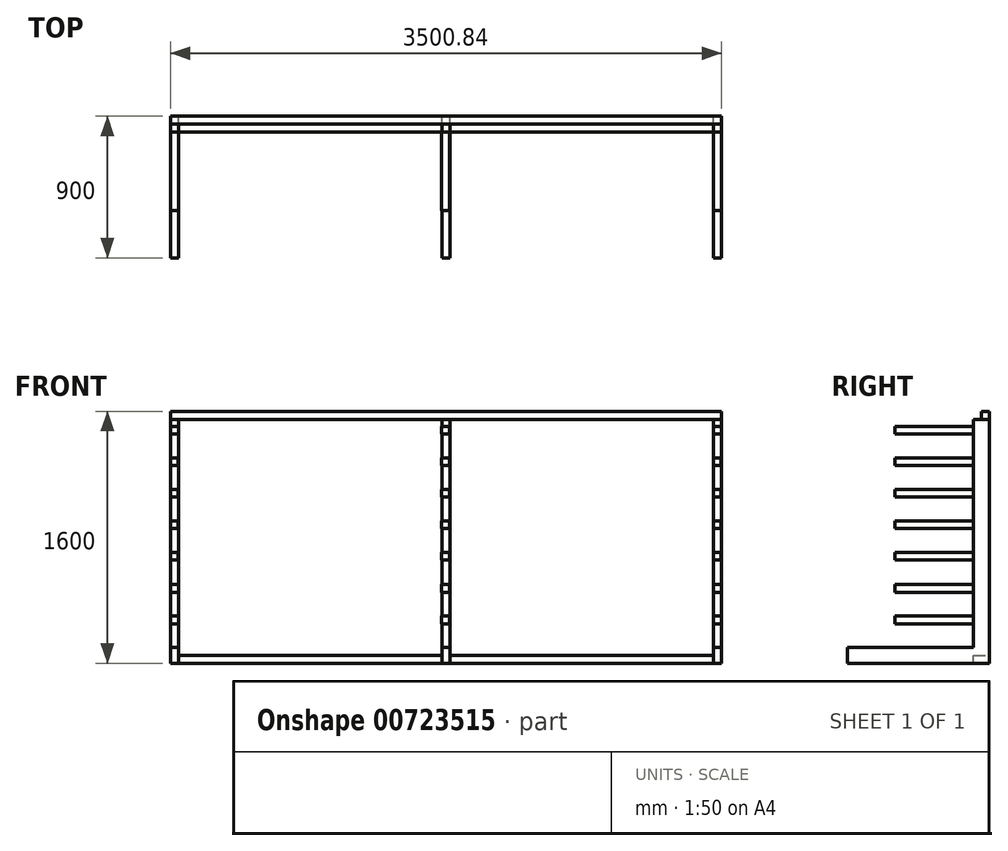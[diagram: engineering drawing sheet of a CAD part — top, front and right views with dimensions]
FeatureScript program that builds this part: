
annotation { "Feature Type Name" : "Feature", "Feature Type Description" : "" }
export const myFeature = defineFeature(function(context is Context, id is Id, definition is map)
    precondition{}
    {
        {
            var Q0;
            Q0=qCreatedBy(makeId("Front.planeOp"),FACE);
            var sketch = newSketch(context, id + "F0", { "sketchPlane" : qUnion([Q0])});
            skLineSegment(sketch, "E0.bottom", {"start": v(0, 0) * mm, "end": v(-3500, 0) * mm});
            skLineSegment(sketch, "E0.left", {"start": v(0, 0) * mm, "end": v(0, 1550) * mm});
            skLineSegment(sketch, "E0.right", {"start": v(-3500, 0) * mm, "end": v(-3500, 1550) * mm});
            skLineSegment(sketch, "E1.1", {"start": v(-50, 50) * mm, "end": v(-50, 1550) * mm});
            skLineSegment(sketch, "E1.2", {"start": v(-50, 50) * mm, "end": v(-1725, 50) * mm});
            skLineSegment(sketch, "E1.3", {"start": v(-3450, 50) * mm, "end": v(-3450, 1550) * mm});
            skPoint(sketch, "E2", {"position": v(-1775, 50) * mm});
            skPoint(sketch, "E3", {"position": v(-1725, 50) * mm});
            skLineSegment(sketch, "E4", {"start": v(-1775, 50) * mm, "end": v(-1775, 1550) * mm});
            skLineSegment(sketch, "E5.0", {"start": v(-1725, 50) * mm, "end": v(-1725, 1550) * mm});
            skLineSegment(sketch, "E6.trimOffspring", {"start": v(-1775, 50) * mm, "end": v(-3450, 50) * mm});
            skLineSegment(sketch, "E7", {"start": v(-3450, 1550) * mm, "end": v(-3500, 1550) * mm});
            skLineSegment(sketch, "E8", {"start": v(-1775, 1550) * mm, "end": v(-1725, 1550) * mm});
            skLineSegment(sketch, "E9", {"start": v(-50, 1550) * mm, "end": v(0, 1550) * mm});
            skSolve(sketch);
        }
        {
            var Q0;
            Q0=makeQuery(id+"F0.imprint","IMPRINT",FACE,{"disambiguationData":[TD([[makeQuery(id+"F0.imprint","IMPRINT",EDGE,{"derivedFrom":sQuery(id+"F0.wireOp",EDGE,"E0.bottom")}),-1.0]])]});
            extrude(context, id + "F1", {"entities" : qUnion([Q0]), "depth" : 100 * mm, "offsetDistance" : 25 * mm});
        }
        {
            var Q0;
            Q0=makeQuery(id+"F1.opExtrude","CAP_FACE",FACE,{"disambiguationData":[OSD([sQuery(id+"F0.wireOp",EDGE,"E0.bottom"),sQuery(id+"F0.wireOp",EDGE,"E0.left"),sQuery(id+"F0.wireOp",EDGE,"E0.right"),sQuery(id+"F0.wireOp",EDGE,"E1.1"),sQuery(id+"F0.wireOp",EDGE,"E1.2"),sQuery(id+"F0.wireOp",EDGE,"E1.3"),sQuery(id+"F0.wireOp",EDGE,"E4"),sQuery(id+"F0.wireOp",EDGE,"E5.0"),sQuery(id+"F0.wireOp",EDGE,"E6.trimOffspring"),sQuery(id+"F0.wireOp",EDGE,"E7"),sQuery(id+"F0.wireOp",EDGE,"E8"),sQuery(id+"F0.wireOp",EDGE,"E9")])],"isStart":false});
            var sketch = newSketch(context, id + "F2", { "sketchPlane" : qUnion([Q0])});
            skLineSegment(sketch, "E10.bottom", {"start": v(-3500, 0) * mm, "end": v(-3450, 0) * mm});
            skLineSegment(sketch, "E10.top", {"start": v(-3500, 100) * mm, "end": v(-3450, 100) * mm});
            skLineSegment(sketch, "E10.left", {"start": v(-3500, 0) * mm, "end": v(-3500, 100) * mm});
            skLineSegment(sketch, "E10.right", {"start": v(-3450, 0) * mm, "end": v(-3450, 100) * mm});
            skLineSegment(sketch, "E11.bottom", {"start": v(-1775, 0) * mm, "end": v(-1725, 0) * mm});
            skLineSegment(sketch, "E11.top", {"start": v(-1775, 100) * mm, "end": v(-1725, 100) * mm});
            skLineSegment(sketch, "E11.left", {"start": v(-1775, 0) * mm, "end": v(-1775, 100) * mm});
            skLineSegment(sketch, "E11.right", {"start": v(-1725, 0) * mm, "end": v(-1725, 100) * mm});
            skLineSegment(sketch, "E12.bottom", {"start": v(0, 0) * mm, "end": v(-50, 0) * mm});
            skLineSegment(sketch, "E12.top", {"start": v(0, 100) * mm, "end": v(-50, 100) * mm});
            skLineSegment(sketch, "E12.left", {"start": v(0, 0) * mm, "end": v(0, 100) * mm});
            skLineSegment(sketch, "E12.right", {"start": v(-50, 0) * mm, "end": v(-50, 100) * mm});
            skSolve(sketch);
        }
        {
            var Q0;
            {var subQ2=sQuery(id+"F2.wireOp",EDGE,"E11.bottom");Q0=makeQuery(id+"F2.imprint","IMPRINT",FACE,{"disambiguationData":[TD([[makeQuery(id+"F2.imprint","IMPRINT",EDGE,{"derivedFrom":subQ2}),-1.0]])]});}
            var Q1;
            {var subQ3=sQuery(id+"F2.wireOp",EDGE,"E10.bottom");Q1=makeQuery(id+"F2.imprint","IMPRINT",FACE,{"disambiguationData":[TD([[makeQuery(id+"F2.imprint","IMPRINT",EDGE,{"derivedFrom":subQ3}),-1.0]])]});}
            var Q2;
            {var subQ3=sQuery(id+"F2.wireOp",EDGE,"E12.bottom");Q2=makeQuery(id+"F2.imprint","IMPRINT",FACE,{"disambiguationData":[TD([[makeQuery(id+"F2.imprint","IMPRINT",EDGE,{"derivedFrom":subQ3}),-1.0]])]});}
            extrude(context, id + "F3", {"entities" : qUnion([Q0, Q1, Q2]), "operationType" : NewBodyOperationType.ADD, "depth" : 800 * mm, "offsetDistance" : 25 * mm});
        }
        {
            var Q0;
            Q0=makeQuery(id+"F1.opExtrude","SWEPT_FACE",FACE,{"disambiguationData":[OSD([sQuery(id+"F0.wireOp",EDGE,"E8")])]});
            var sketch = newSketch(context, id + "F4", { "sketchPlane" : qUnion([Q0])});
            skPoint(sketch, "E13", {"position": v(-1750, 0) * mm});
            skPoint(sketch, "E14", {"position": v(-1750, -100) * mm});
            skLineSegment(sketch, "E15", {"start": v(-1750, 0) * mm, "end": v(-1750, -50) * mm});
            skLineSegment(sketch, "E16.bottom", {"start": v(-1750, -50) * mm, "end": v(-3499.82, -50) * mm});
            skLineSegment(sketch, "E16.top", {"start": v(-1750, 0) * mm, "end": v(-3499.82, 0) * mm});
            skLineSegment(sketch, "E16.left", {"start": v(-1750, -50) * mm, "end": v(-1750, 0) * mm});
            skLineSegment(sketch, "E16.right", {"start": v(-3499.82, -50) * mm, "end": v(-3499.82, 0) * mm});
            skLineSegment(sketch, "E17.MirrorCS", {"start": v(-1750, 0) * mm, "end": v(-0.18, 0) * mm});
            skLineSegment(sketch, "E18.MirrorCS", {"start": v(-1750, -50) * mm, "end": v(-0.18, -50) * mm});
            skLineSegment(sketch, "E19.MirrorCS", {"start": v(-0.18, -50) * mm, "end": v(-0.18, 0) * mm});
            skSolve(sketch);
        }
        {
            var Q0;
            Q0=qSketchRegion(id+"F4",true);
            extrude(context, id + "F5", {"entities" : qUnion([Q0]), "operationType" : NewBodyOperationType.ADD, "depth" : 50 * mm, "offsetDistance" : 25 * mm});
        }
        {
            var Q0;
            {var subQ0=sQuery(id+"F0.wireOp",EDGE,"E0.right");var subQ1=sQuery(id+"F0.wireOp",EDGE,"E7");var subQ2=sQuery(id+"F0.wireOp",EDGE,"E1.3");Q0=makeQuery(id+"F3.boolean.opBoolean","SPLIT",FACE,{"disambiguationData":[TD([makeQuery(id+"F1.opExtrude","SWEPT_FACE",FACE,{"disambiguationData":[OSD([subQ0])]})])],"derivedFrom":makeQuery(id+"F1.opExtrude","CAP_FACE",FACE,{"disambiguationData":[OSD([sQuery(id+"F0.wireOp",EDGE,"E0.bottom"),sQuery(id+"F0.wireOp",EDGE,"E0.left"),subQ0,sQuery(id+"F0.wireOp",EDGE,"E1.1"),sQuery(id+"F0.wireOp",EDGE,"E1.2"),subQ2,sQuery(id+"F0.wireOp",EDGE,"E4"),sQuery(id+"F0.wireOp",EDGE,"E5.0"),sQuery(id+"F0.wireOp",EDGE,"E6.trimOffspring"),subQ1,sQuery(id+"F0.wireOp",EDGE,"E8"),sQuery(id+"F0.wireOp",EDGE,"E9")])],"isStart":false})});}
            var sketch = newSketch(context, id + "F6", { "sketchPlane" : qUnion([Q0])});
            skLineSegment(sketch, "E20.bottom", {"start": v(-3500, 250) * mm, "end": v(-3450, 250) * mm});
            skLineSegment(sketch, "E20.top", {"start": v(-3500, 300) * mm, "end": v(-3450, 300) * mm});
            skLineSegment(sketch, "E20.left", {"start": v(-3500, 250) * mm, "end": v(-3500, 300) * mm});
            skLineSegment(sketch, "E20.right", {"start": v(-3450, 250) * mm, "end": v(-3450, 300) * mm});
            skPoint(sketch, "E21", {"position": v(-3500, 450) * mm});
            skLineSegment(sketch, "E22.bottom", {"start": v(-3500, 450) * mm, "end": v(-3450, 450) * mm});
            skLineSegment(sketch, "E22.top", {"start": v(-3500, 500) * mm, "end": v(-3450, 500) * mm});
            skLineSegment(sketch, "E22.left", {"start": v(-3500, 450) * mm, "end": v(-3500, 500) * mm});
            skLineSegment(sketch, "E22.right", {"start": v(-3450, 450) * mm, "end": v(-3450, 500) * mm});
            skPoint(sketch, "E23", {"position": v(-3500, 650) * mm});
            skPoint(sketch, "E24", {"position": v(-3500.84, 655.24) * mm});
            skPoint(sketch, "E25", {"position": v(-3500.84, 855.24) * mm});
            skPoint(sketch, "E26", {"position": v(-3500.84, 1055.24) * mm});
            skPoint(sketch, "E27", {"position": v(-3500.84, 1255.24) * mm});
            skLineSegment(sketch, "E28.bottom", {"start": v(-3500.84, 655.24) * mm, "end": v(-3450.84, 655.24) * mm});
            skLineSegment(sketch, "E28.top", {"start": v(-3500.84, 705.24) * mm, "end": v(-3450.84, 705.24) * mm});
            skLineSegment(sketch, "E28.left", {"start": v(-3500.84, 655.24) * mm, "end": v(-3500.84, 705.24) * mm});
            skLineSegment(sketch, "E28.right", {"start": v(-3450.84, 655.24) * mm, "end": v(-3450.84, 705.24) * mm});
            skLineSegment(sketch, "E29.bottom", {"start": v(-3500.84, 855.24) * mm, "end": v(-3450.84, 855.24) * mm});
            skLineSegment(sketch, "E29.top", {"start": v(-3500.84, 905.24) * mm, "end": v(-3450.84, 905.24) * mm});
            skLineSegment(sketch, "E29.left", {"start": v(-3500.84, 855.24) * mm, "end": v(-3500.84, 905.24) * mm});
            skLineSegment(sketch, "E29.right", {"start": v(-3450.84, 855.24) * mm, "end": v(-3450.84, 905.24) * mm});
            skLineSegment(sketch, "E30.bottom", {"start": v(-3500.84, 1055.24) * mm, "end": v(-3450.84, 1055.24) * mm});
            skLineSegment(sketch, "E30.top", {"start": v(-3500.84, 1105.24) * mm, "end": v(-3450.84, 1105.24) * mm});
            skLineSegment(sketch, "E30.left", {"start": v(-3500.84, 1055.24) * mm, "end": v(-3500.84, 1105.24) * mm});
            skLineSegment(sketch, "E30.right", {"start": v(-3450.84, 1055.24) * mm, "end": v(-3450.84, 1105.24) * mm});
            skLineSegment(sketch, "E31.bottom", {"start": v(-3500.84, 1255.24) * mm, "end": v(-3450.84, 1255.24) * mm});
            skLineSegment(sketch, "E31.top", {"start": v(-3500.84, 1305.24) * mm, "end": v(-3450.84, 1305.24) * mm});
            skLineSegment(sketch, "E31.left", {"start": v(-3500.84, 1255.24) * mm, "end": v(-3500.84, 1305.24) * mm});
            skLineSegment(sketch, "E31.right", {"start": v(-3450.84, 1255.24) * mm, "end": v(-3450.84, 1305.24) * mm});
            skPoint(sketch, "E32", {"position": v(-3500, 1455.24) * mm});
            skLineSegment(sketch, "E33.bottom", {"start": v(-3500, 1455.24) * mm, "end": v(-3450, 1455.24) * mm});
            skLineSegment(sketch, "E33.top", {"start": v(-3500, 1505.24) * mm, "end": v(-3450, 1505.24) * mm});
            skLineSegment(sketch, "E33.left", {"start": v(-3500, 1455.24) * mm, "end": v(-3500, 1505.24) * mm});
            skLineSegment(sketch, "E33.right", {"start": v(-3450, 1455.24) * mm, "end": v(-3450, 1505.24) * mm});
            skPoint(sketch, "E34", {"position": v(-52.24, 250) * mm});
            skPoint(sketch, "E35", {"position": v(-1777.89, 250) * mm});
            skLineSegment(sketch, "E36.bottom", {"start": v(-1777.89, 250) * mm, "end": v(-1727.89, 250) * mm});
            skLineSegment(sketch, "E36.top", {"start": v(-1777.89, 300) * mm, "end": v(-1727.89, 300) * mm});
            skLineSegment(sketch, "E36.left", {"start": v(-1777.89, 250) * mm, "end": v(-1777.89, 300) * mm});
            skLineSegment(sketch, "E36.right", {"start": v(-1727.89, 250) * mm, "end": v(-1727.89, 300) * mm});
            skPoint(sketch, "E37", {"position": v(-1777.89, 450) * mm});
            skLineSegment(sketch, "E38.bottom", {"start": v(-1777.89, 450) * mm, "end": v(-1727.89, 450) * mm});
            skLineSegment(sketch, "E38.top", {"start": v(-1777.89, 500) * mm, "end": v(-1727.89, 500) * mm});
            skLineSegment(sketch, "E38.left", {"start": v(-1777.89, 450) * mm, "end": v(-1777.89, 500) * mm});
            skLineSegment(sketch, "E38.right", {"start": v(-1727.89, 450) * mm, "end": v(-1727.89, 500) * mm});
            skPoint(sketch, "E39", {"position": v(-1777.89, 650) * mm});
            skPoint(sketch, "E40", {"position": v(-1778.73, 655.24) * mm});
            skPoint(sketch, "E41", {"position": v(-1778.73, 855.24) * mm});
            skPoint(sketch, "E42", {"position": v(-1778.73, 1055.24) * mm});
            skPoint(sketch, "E43", {"position": v(-1778.73, 1255.24) * mm});
            skLineSegment(sketch, "E44.bottom", {"start": v(-1778.73, 655.24) * mm, "end": v(-1728.73, 655.24) * mm});
            skLineSegment(sketch, "E44.top", {"start": v(-1778.73, 705.24) * mm, "end": v(-1728.73, 705.24) * mm});
            skLineSegment(sketch, "E44.left", {"start": v(-1778.73, 655.24) * mm, "end": v(-1778.73, 705.24) * mm});
            skLineSegment(sketch, "E44.right", {"start": v(-1728.73, 655.24) * mm, "end": v(-1728.73, 705.24) * mm});
            skLineSegment(sketch, "E45.bottom", {"start": v(-1778.73, 855.24) * mm, "end": v(-1728.73, 855.24) * mm});
            skLineSegment(sketch, "E45.top", {"start": v(-1778.73, 905.24) * mm, "end": v(-1728.73, 905.24) * mm});
            skLineSegment(sketch, "E45.left", {"start": v(-1778.73, 855.24) * mm, "end": v(-1778.73, 905.24) * mm});
            skLineSegment(sketch, "E45.right", {"start": v(-1728.73, 855.24) * mm, "end": v(-1728.73, 905.24) * mm});
            skLineSegment(sketch, "E46.bottom", {"start": v(-1778.73, 1055.24) * mm, "end": v(-1728.73, 1055.24) * mm});
            skLineSegment(sketch, "E46.top", {"start": v(-1778.73, 1105.24) * mm, "end": v(-1728.73, 1105.24) * mm});
            skLineSegment(sketch, "E46.left", {"start": v(-1778.73, 1055.24) * mm, "end": v(-1778.73, 1105.24) * mm});
            skLineSegment(sketch, "E46.right", {"start": v(-1728.73, 1055.24) * mm, "end": v(-1728.73, 1105.24) * mm});
            skLineSegment(sketch, "E47.bottom", {"start": v(-1778.73, 1255.24) * mm, "end": v(-1728.73, 1255.24) * mm});
            skLineSegment(sketch, "E47.top", {"start": v(-1778.73, 1305.24) * mm, "end": v(-1728.73, 1305.24) * mm});
            skLineSegment(sketch, "E47.left", {"start": v(-1778.73, 1255.24) * mm, "end": v(-1778.73, 1305.24) * mm});
            skLineSegment(sketch, "E47.right", {"start": v(-1728.73, 1255.24) * mm, "end": v(-1728.73, 1305.24) * mm});
            skPoint(sketch, "E48", {"position": v(-1777.89, 1455.24) * mm});
            skLineSegment(sketch, "E49.bottom", {"start": v(-1777.89, 1455.24) * mm, "end": v(-1727.89, 1455.24) * mm});
            skLineSegment(sketch, "E49.top", {"start": v(-1777.89, 1505.24) * mm, "end": v(-1727.89, 1505.24) * mm});
            skLineSegment(sketch, "E49.left", {"start": v(-1777.89, 1455.24) * mm, "end": v(-1777.89, 1505.24) * mm});
            skLineSegment(sketch, "E49.right", {"start": v(-1727.89, 1455.24) * mm, "end": v(-1727.89, 1505.24) * mm});
            skLineSegment(sketch, "E50.bottom", {"start": v(-52.24, 250) * mm, "end": v(-2.24, 250) * mm});
            skLineSegment(sketch, "E50.top", {"start": v(-52.24, 300) * mm, "end": v(-2.24, 300) * mm});
            skLineSegment(sketch, "E50.left", {"start": v(-52.24, 250) * mm, "end": v(-52.24, 300) * mm});
            skLineSegment(sketch, "E50.right", {"start": v(-2.24, 250) * mm, "end": v(-2.24, 300) * mm});
            skPoint(sketch, "E51", {"position": v(-52.24, 450) * mm});
            skLineSegment(sketch, "E52.bottom", {"start": v(-52.24, 450) * mm, "end": v(-2.24, 450) * mm});
            skLineSegment(sketch, "E52.top", {"start": v(-52.24, 500) * mm, "end": v(-2.24, 500) * mm});
            skLineSegment(sketch, "E52.left", {"start": v(-52.24, 450) * mm, "end": v(-52.24, 500) * mm});
            skLineSegment(sketch, "E52.right", {"start": v(-2.24, 450) * mm, "end": v(-2.24, 500) * mm});
            skPoint(sketch, "E53", {"position": v(-52.24, 650) * mm});
            skPoint(sketch, "E54", {"position": v(-53.08, 655.24) * mm});
            skPoint(sketch, "E55", {"position": v(-53.08, 855.24) * mm});
            skPoint(sketch, "E56", {"position": v(-53.08, 1055.24) * mm});
            skPoint(sketch, "E57", {"position": v(-53.08, 1255.24) * mm});
            skLineSegment(sketch, "E58.bottom", {"start": v(-53.08, 655.24) * mm, "end": v(-3.08, 655.24) * mm});
            skLineSegment(sketch, "E58.top", {"start": v(-53.08, 705.24) * mm, "end": v(-3.08, 705.24) * mm});
            skLineSegment(sketch, "E58.left", {"start": v(-53.08, 655.24) * mm, "end": v(-53.08, 705.24) * mm});
            skLineSegment(sketch, "E58.right", {"start": v(-3.08, 655.24) * mm, "end": v(-3.08, 705.24) * mm});
            skLineSegment(sketch, "E59.bottom", {"start": v(-53.08, 855.24) * mm, "end": v(-3.08, 855.24) * mm});
            skLineSegment(sketch, "E59.top", {"start": v(-53.08, 905.24) * mm, "end": v(-3.08, 905.24) * mm});
            skLineSegment(sketch, "E59.left", {"start": v(-53.08, 855.24) * mm, "end": v(-53.08, 905.24) * mm});
            skLineSegment(sketch, "E59.right", {"start": v(-3.08, 855.24) * mm, "end": v(-3.08, 905.24) * mm});
            skLineSegment(sketch, "E60.bottom", {"start": v(-53.08, 1055.24) * mm, "end": v(-3.08, 1055.24) * mm});
            skLineSegment(sketch, "E60.top", {"start": v(-53.08, 1105.24) * mm, "end": v(-3.08, 1105.24) * mm});
            skLineSegment(sketch, "E60.left", {"start": v(-53.08, 1055.24) * mm, "end": v(-53.08, 1105.24) * mm});
            skLineSegment(sketch, "E60.right", {"start": v(-3.08, 1055.24) * mm, "end": v(-3.08, 1105.24) * mm});
            skLineSegment(sketch, "E61.bottom", {"start": v(-53.08, 1255.24) * mm, "end": v(-3.08, 1255.24) * mm});
            skLineSegment(sketch, "E61.top", {"start": v(-53.08, 1305.24) * mm, "end": v(-3.08, 1305.24) * mm});
            skLineSegment(sketch, "E61.left", {"start": v(-53.08, 1255.24) * mm, "end": v(-53.08, 1305.24) * mm});
            skLineSegment(sketch, "E61.right", {"start": v(-3.08, 1255.24) * mm, "end": v(-3.08, 1305.24) * mm});
            skPoint(sketch, "E62", {"position": v(-52.24, 1455.24) * mm});
            skLineSegment(sketch, "E63.bottom", {"start": v(-52.24, 1455.24) * mm, "end": v(-2.24, 1455.24) * mm});
            skLineSegment(sketch, "E63.top", {"start": v(-52.24, 1505.24) * mm, "end": v(-2.24, 1505.24) * mm});
            skLineSegment(sketch, "E63.left", {"start": v(-52.24, 1455.24) * mm, "end": v(-52.24, 1505.24) * mm});
            skLineSegment(sketch, "E63.right", {"start": v(-2.24, 1455.24) * mm, "end": v(-2.24, 1505.24) * mm});
            skSolve(sketch);
        }
        {
            var Q0;
            Q0=qSketchRegion(id+"F6",true);
            extrude(context, id + "F7", {"entities" : qUnion([Q0]), "operationType" : NewBodyOperationType.ADD, "depth" : 500 * mm, "offsetDistance" : 25 * mm});
        }
        {
            var Q0;
            Q0=qSketchRegion(id+"F6",true);
            extrude(context, id + "F8", {"entities" : qUnion([Q0]), "operationType" : NewBodyOperationType.ADD, "depth" : 25 * mm, "offsetDistance" : 25 * mm});
        }
    });
